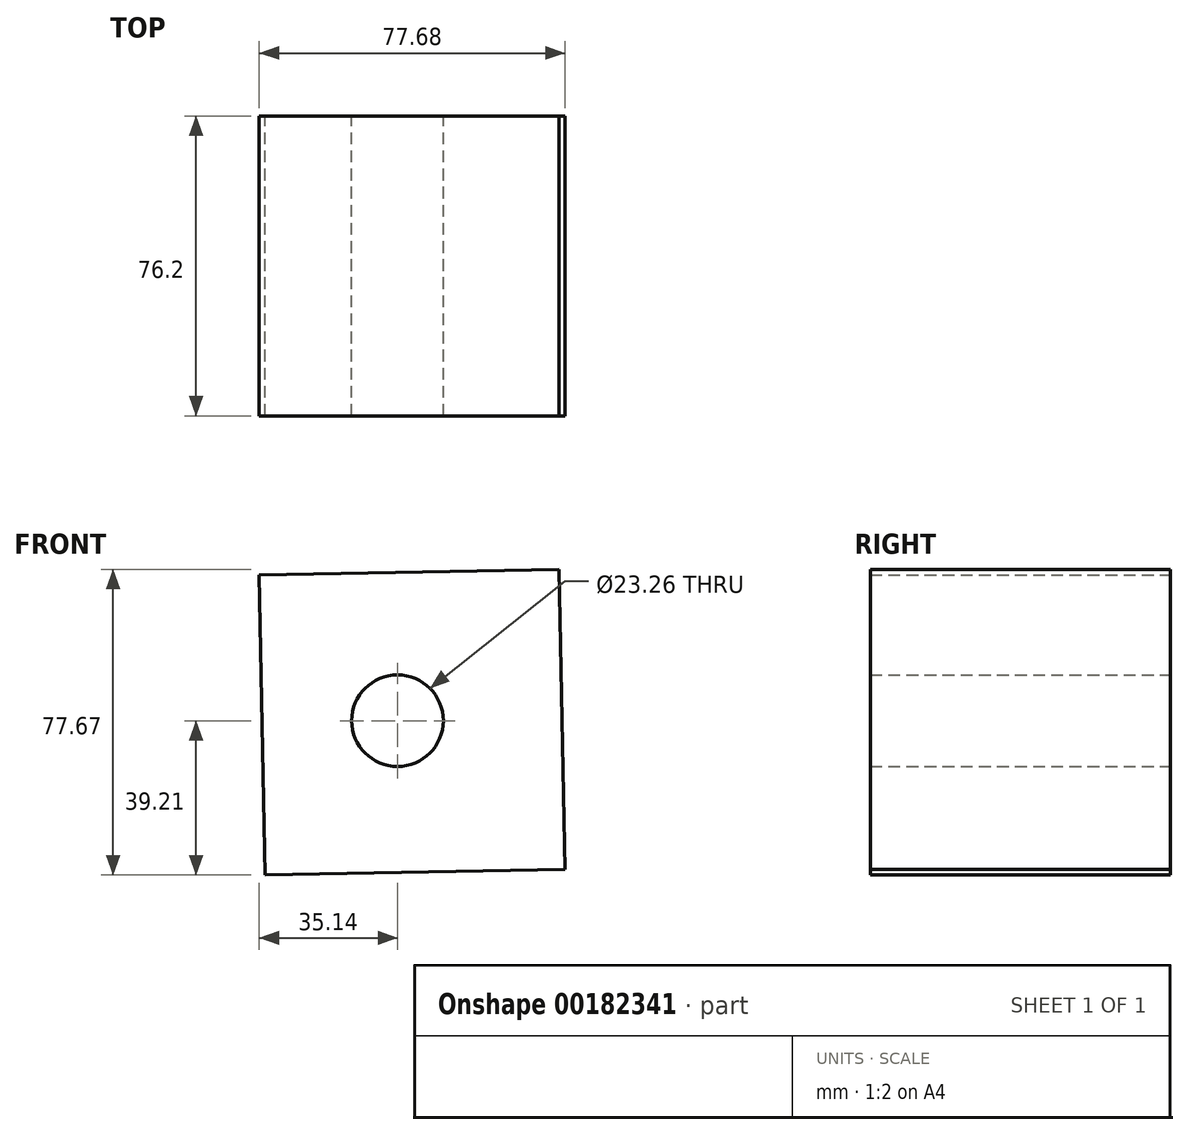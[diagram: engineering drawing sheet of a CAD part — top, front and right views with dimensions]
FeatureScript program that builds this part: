
annotation { "Feature Type Name" : "Feature", "Feature Type Description" : "" }
export const myFeature = defineFeature(function(context is Context, id is Id, definition is map)
    precondition{}
    {
        {
            var Q0;
            Q0=qCreatedBy(makeId("Front.planeOp"),FACE);
            var sketch = newSketch(context, id + "F0", { "sketchPlane" : qUnion([Q0])});
            skLineSegment(sketch, "E0", {"start": v(-35.14, 36.97) * mm, "end": v(-33.65, -39.21) * mm});
            skLineSegment(sketch, "E1", {"start": v(-33.65, -39.21) * mm, "end": v(42.54, -37.72) * mm});
            skLineSegment(sketch, "E2", {"start": v(42.54, -37.72) * mm, "end": v(41.05, 38.46) * mm});
            skLineSegment(sketch, "E3", {"start": v(41.05, 38.46) * mm, "end": v(-35.14, 36.97) * mm});
            skSolve(sketch);
        }
        {
            var Q0;
            Q0=makeQuery(id+"F0.imprint","IMPRINT",FACE,{"disambiguationData":[TD([[makeQuery(id+"F0.imprint","IMPRINT",EDGE,{"derivedFrom":sQuery(id+"F0.wireOp",EDGE,"E0")}),1.0]])]});
            extrude(context, id + "F1", {"entities" : qUnion([Q0]), "depth" : 76.2 * mm});
        }
        {
            var Q0;
            Q0=qCreatedBy(makeId("Front.planeOp"),FACE);
            var sketch = newSketch(context, id + "F2", { "sketchPlane" : qUnion([Q0])});
            skCircle(sketch, "E4", {"center": v(0, 0) * mm, "radius": 11.63 * mm});
            skSolve(sketch);
        }
        {
            var Q0;
            Q0=makeQuery(id+"F2.imprint","IMPRINT",FACE,{"disambiguationData":[TD([[makeQuery(id+"F2.imprint","IMPRINT",EDGE,{"derivedFrom":sQuery(id+"F2.wireOp",EDGE,"E4")}),1.0]])]});
            var Q1;
            Q1=sQuery(id+"F2.wireOp",EDGE,"E4");
            extrude(context, id + "F3", {"entities" : qUnion([Q0]), "operationType" : NewBodyOperationType.REMOVE, "surfaceEntities" : qUnion([Q1]), "depth" : 84.58 * mm});
        }
    });
